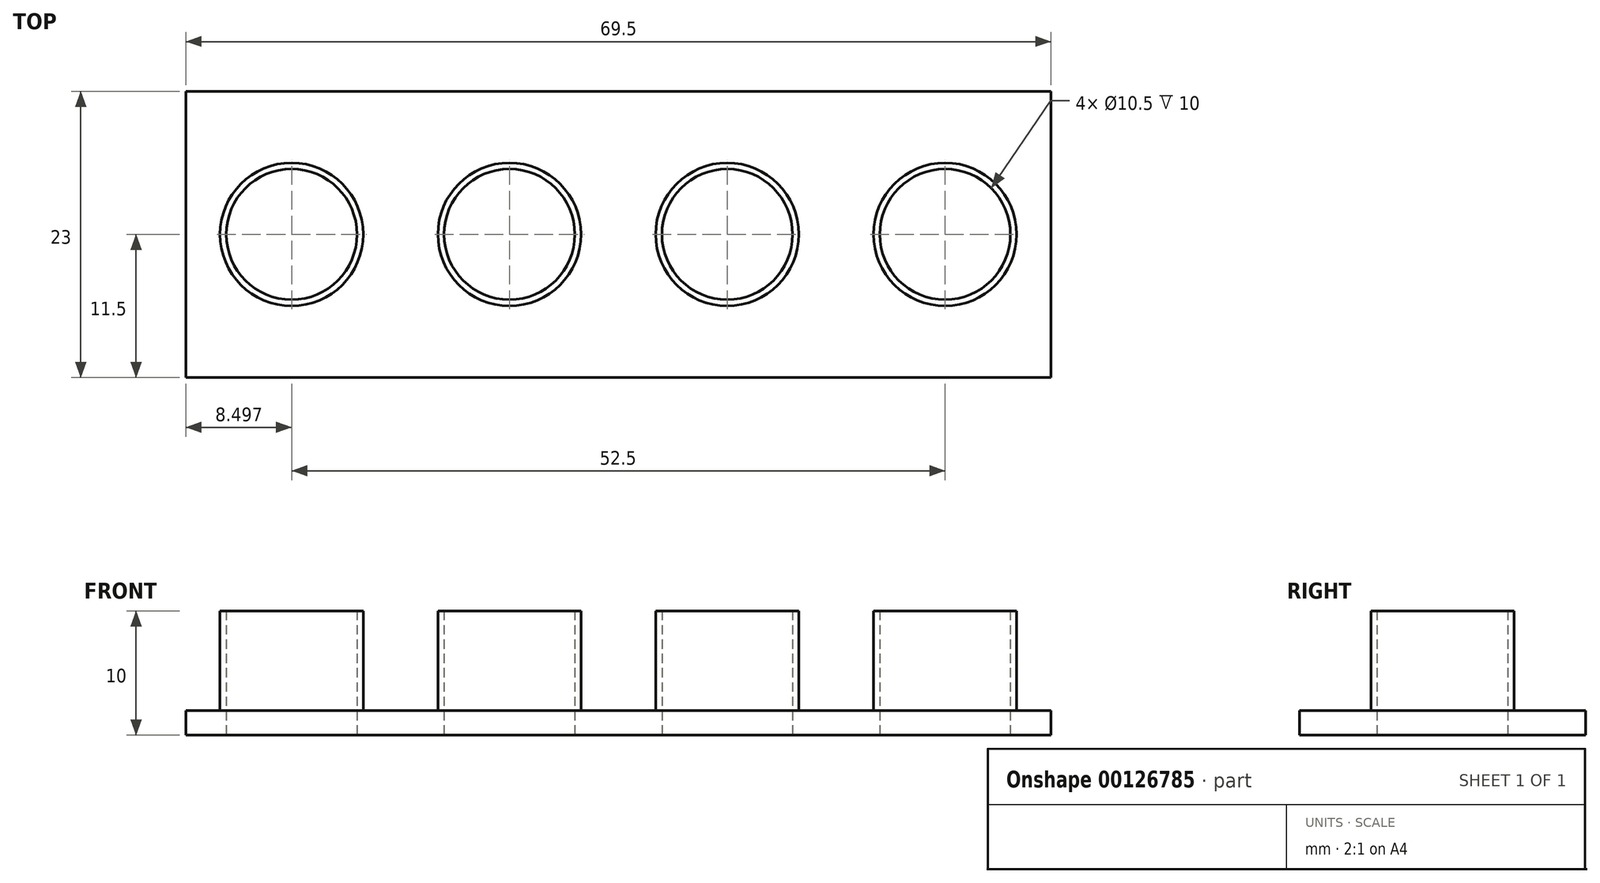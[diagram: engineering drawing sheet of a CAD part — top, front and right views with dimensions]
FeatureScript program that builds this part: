
annotation { "Feature Type Name" : "Feature", "Feature Type Description" : "" }
export const myFeature = defineFeature(function(context is Context, id is Id, definition is map)
    precondition{}
    {
        {
            var Q0;
            Q0=qCreatedBy(makeId("Top.planeOp"),FACE);
            var sketch = newSketch(context, id + "F0", { "sketchPlane" : qUnion([Q0])});
            skLineSegment(sketch, "E0.bottom", {"start": v(-29.8, 7) * mm, "end": v(-15.8, 7) * mm});
            skLineSegment(sketch, "E0.top", {"start": v(-29.8, -13) * mm, "end": v(-15.8, -13) * mm});
            skLineSegment(sketch, "E0.left", {"start": v(-29.8, 7) * mm, "end": v(-29.8, -13) * mm});
            skLineSegment(sketch, "E0.right", {"start": v(36.7, 7) * mm, "end": v(36.7, -13) * mm});
            skLineSegment(sketch, "E1.top", {"start": v(-15.8, 3) * mm, "end": v(-14.8, 3) * mm});
            skLineSegment(sketch, "E1.left", {"start": v(-15.8, 7) * mm, "end": v(-15.8, 3) * mm});
            skLineSegment(sketch, "E1.right", {"start": v(-14.8, 7) * mm, "end": v(-14.8, 3) * mm});
            skLineSegment(sketch, "E2.top", {"start": v(-13.3, 3) * mm, "end": v(-12.3, 3) * mm});
            skLineSegment(sketch, "E2.left", {"start": v(-13.3, 7) * mm, "end": v(-13.3, 3) * mm});
            skLineSegment(sketch, "E2.right", {"start": v(-12.3, 7) * mm, "end": v(-12.3, 3) * mm});
            skLineSegment(sketch, "E3.top", {"start": v(4.2, 3) * mm, "end": v(5.2, 3) * mm});
            skLineSegment(sketch, "E3.left", {"start": v(4.2, 7) * mm, "end": v(4.2, 3) * mm});
            skLineSegment(sketch, "E3.right", {"start": v(5.2, 7) * mm, "end": v(5.2, 3) * mm});
            skLineSegment(sketch, "E4.top", {"start": v(19.2, 3) * mm, "end": v(20.2, 3) * mm});
            skLineSegment(sketch, "E4.left", {"start": v(19.2, 7) * mm, "end": v(19.2, 3) * mm});
            skLineSegment(sketch, "E4.right", {"start": v(20.2, 7) * mm, "end": v(20.2, 3) * mm});
            skLineSegment(sketch, "E5.top", {"start": v(21.7, 3) * mm, "end": v(22.7, 3) * mm});
            skLineSegment(sketch, "E5.left", {"start": v(21.7, 7) * mm, "end": v(21.7, 3) * mm});
            skLineSegment(sketch, "E5.right", {"start": v(22.7, 7) * mm, "end": v(22.7, 3) * mm});
            skLineSegment(sketch, "E6.top", {"start": v(-15.8, -9) * mm, "end": v(-14.8, -9) * mm});
            skLineSegment(sketch, "E6.left", {"start": v(-15.8, -13) * mm, "end": v(-15.8, -9) * mm});
            skLineSegment(sketch, "E6.right", {"start": v(-14.8, -13) * mm, "end": v(-14.8, -9) * mm});
            skLineSegment(sketch, "E7.top", {"start": v(-13.3, -9) * mm, "end": v(-12.3, -9) * mm});
            skLineSegment(sketch, "E7.left", {"start": v(-13.3, -13) * mm, "end": v(-13.3, -9) * mm});
            skLineSegment(sketch, "E7.right", {"start": v(-12.3, -13) * mm, "end": v(-12.3, -9) * mm});
            skLineSegment(sketch, "E8.top", {"start": v(1.7, -9) * mm, "end": v(2.7, -9) * mm});
            skLineSegment(sketch, "E8.left", {"start": v(1.7, -13) * mm, "end": v(1.7, -9) * mm});
            skLineSegment(sketch, "E8.right", {"start": v(2.7, -13) * mm, "end": v(2.7, -9) * mm});
            skLineSegment(sketch, "E9.top", {"start": v(4.2, -9) * mm, "end": v(5.2, -9) * mm});
            skLineSegment(sketch, "E9.left", {"start": v(4.2, -13) * mm, "end": v(4.2, -9) * mm});
            skLineSegment(sketch, "E9.right", {"start": v(5.2, -13) * mm, "end": v(5.2, -9) * mm});
            skLineSegment(sketch, "E10.top", {"start": v(19.2, -9) * mm, "end": v(20.2, -9) * mm});
            skLineSegment(sketch, "E10.left", {"start": v(19.2, -13) * mm, "end": v(19.2, -9) * mm});
            skLineSegment(sketch, "E10.right", {"start": v(20.2, -13) * mm, "end": v(20.2, -9) * mm});
            skLineSegment(sketch, "E11.top", {"start": v(21.7, -9) * mm, "end": v(22.7, -9) * mm});
            skLineSegment(sketch, "E11.left", {"start": v(21.7, -13) * mm, "end": v(21.7, -9) * mm});
            skLineSegment(sketch, "E11.right", {"start": v(22.7, -13) * mm, "end": v(22.7, -9) * mm});
            skLineSegment(sketch, "E12.top", {"start": v(1.7, 3) * mm, "end": v(2.7, 3) * mm});
            skLineSegment(sketch, "E12.left", {"start": v(1.7, 7) * mm, "end": v(1.7, 3) * mm});
            skLineSegment(sketch, "E12.right", {"start": v(2.7, 7) * mm, "end": v(2.7, 3) * mm});
            skLineSegment(sketch, "E13.trimOffspring", {"start": v(-14.8, 7) * mm, "end": v(-13.3, 7) * mm});
            skLineSegment(sketch, "E14.trimOffspring", {"start": v(-12.3, 7) * mm, "end": v(1.7, 7) * mm});
            skLineSegment(sketch, "E15.trimOffspring", {"start": v(2.7, 7) * mm, "end": v(4.2, 7) * mm});
            skLineSegment(sketch, "E16.trimOffspring", {"start": v(5.2, 7) * mm, "end": v(19.2, 7) * mm});
            skLineSegment(sketch, "E17.trimOffspring", {"start": v(-14.8, -13) * mm, "end": v(-13.3, -13) * mm});
            skLineSegment(sketch, "E18.trimOffspring", {"start": v(-12.3, -13) * mm, "end": v(1.7, -13) * mm});
            skLineSegment(sketch, "E19.trimOffspring", {"start": v(2.7, -13) * mm, "end": v(4.2, -13) * mm});
            skLineSegment(sketch, "E20.trimOffspring", {"start": v(5.2, -13) * mm, "end": v(19.2, -13) * mm});
            skLineSegment(sketch, "E21.trimOffspring", {"start": v(20.2, -13) * mm, "end": v(21.7, -13) * mm});
            skLineSegment(sketch, "E22.trimOffspring", {"start": v(22.7, -13) * mm, "end": v(36.7, -13) * mm});
            skLineSegment(sketch, "E23.trimOffspring", {"start": v(20.2, 7) * mm, "end": v(21.7, 7) * mm});
            skLineSegment(sketch, "E24.trimOffspring", {"start": v(22.7, 7) * mm, "end": v(36.7, 7) * mm});
            skLineSegment(sketch, "E25", {"start": v(-29.8, -3) * mm, "end": v(37.18, -3) * mm, "construction": true});
            skLineSegment(sketch, "E26", {"start": v(-22.8, 7) * mm, "end": v(-22.8, -26.1) * mm, "construction": true});
            skLineSegment(sketch, "E27", {"start": v(-5.3, 7) * mm, "end": v(-5.3, -26.98) * mm, "construction": true});
            skLineSegment(sketch, "E28", {"start": v(12.2, 7) * mm, "end": v(12.2, -27.86) * mm, "construction": true});
            skLineSegment(sketch, "E29", {"start": v(29.7, 7) * mm, "end": v(29.7, -23.35) * mm, "construction": true});
            skCircle(sketch, "E30", {"center": v(-22.8, -3) * mm, "radius": 5.25 * mm});
            skCircle(sketch, "E31", {"center": v(-22.8, -3) * mm, "radius": 5.75 * mm});
            skCircle(sketch, "E32", {"center": v(-5.3, -3) * mm, "radius": 5.75 * mm});
            skCircle(sketch, "E33", {"center": v(-5.3, -3) * mm, "radius": 5.25 * mm});
            skCircle(sketch, "E34", {"center": v(12.2, -3) * mm, "radius": 5.75 * mm});
            skCircle(sketch, "E35", {"center": v(12.2, -3) * mm, "radius": 5.25 * mm});
            skCircle(sketch, "E36", {"center": v(29.7, -3) * mm, "radius": 5.75 * mm});
            skCircle(sketch, "E37", {"center": v(29.7, -3) * mm, "radius": 5.25 * mm});
            skLineSegment(sketch, "E38.bottom", {"start": v(-31.3, 8.5) * mm, "end": v(38.2, 8.5) * mm});
            skLineSegment(sketch, "E38.top", {"start": v(-31.3, -14.5) * mm, "end": v(38.2, -14.5) * mm});
            skLineSegment(sketch, "E38.left", {"start": v(-31.3, 8.5) * mm, "end": v(-31.3, -14.5) * mm});
            skLineSegment(sketch, "E38.right", {"start": v(38.2, 8.5) * mm, "end": v(38.2, -14.5) * mm});
            skLineSegment(sketch, "E39", {"start": v(-15.8, 7) * mm, "end": v(-14.8, 7) * mm});
            skLineSegment(sketch, "E40", {"start": v(-13.3, 7) * mm, "end": v(-12.3, 7) * mm});
            skLineSegment(sketch, "E41", {"start": v(1.7, 7) * mm, "end": v(2.7, 7) * mm});
            skLineSegment(sketch, "E42", {"start": v(4.2, 7) * mm, "end": v(5.2, 7) * mm});
            skLineSegment(sketch, "E43", {"start": v(-15.8, -13) * mm, "end": v(-14.8, -13) * mm});
            skLineSegment(sketch, "E44", {"start": v(-13.3, -13) * mm, "end": v(-12.3, -13) * mm});
            skLineSegment(sketch, "E45", {"start": v(1.7, -13) * mm, "end": v(2.7, -13) * mm});
            skLineSegment(sketch, "E46", {"start": v(4.3, -13.03) * mm, "end": v(5.2, -13) * mm});
            skLineSegment(sketch, "E47", {"start": v(19.2, 7) * mm, "end": v(20.2, 7) * mm});
            skLineSegment(sketch, "E48", {"start": v(21.7, 7) * mm, "end": v(22.7, 7) * mm});
            skLineSegment(sketch, "E49", {"start": v(19.2, -13) * mm, "end": v(20.2, -13) * mm});
            skLineSegment(sketch, "E50", {"start": v(21.7, -13) * mm, "end": v(22.7, -13) * mm});
            skSolve(sketch);
        }
        {
            var Q0;
            Q0=makeQuery(id+"F0.imprint","IMPRINT",FACE,{"disambiguationData":[TD([[makeQuery(id+"F0.imprint","IMPRINT",EDGE,{"derivedFrom":sQuery(id+"F0.wireOp",EDGE,"E0.bottom")}),-1.0]])]});
            var Q1;
            Q1=makeQuery(id+"F0.imprint","IMPRINT",FACE,{"disambiguationData":[TD([[makeQuery(id+"F0.imprint","IMPRINT",EDGE,{"derivedFrom":sQuery(id+"F0.wireOp",EDGE,"E1.top")}),1.0]])]});
            var Q2;
            Q2=makeQuery(id+"F0.imprint","IMPRINT",FACE,{"disambiguationData":[TD([[makeQuery(id+"F0.imprint","IMPRINT",EDGE,{"derivedFrom":sQuery(id+"F0.wireOp",EDGE,"E2.top")}),1.0]])]});
            var Q3;
            Q3=makeQuery(id+"F0.imprint","IMPRINT",FACE,{"disambiguationData":[TD([[makeQuery(id+"F0.imprint","IMPRINT",EDGE,{"derivedFrom":sQuery(id+"F0.wireOp",EDGE,"E12.top")}),1.0]])]});
            var Q4;
            Q4=makeQuery(id+"F0.imprint","IMPRINT",FACE,{"disambiguationData":[TD([[makeQuery(id+"F0.imprint","IMPRINT",EDGE,{"derivedFrom":sQuery(id+"F0.wireOp",EDGE,"E3.top")}),1.0]])]});
            var Q5;
            Q5=makeQuery(id+"F0.imprint","IMPRINT",FACE,{"disambiguationData":[TD([[makeQuery(id+"F0.imprint","IMPRINT",EDGE,{"derivedFrom":sQuery(id+"F0.wireOp",EDGE,"E4.top")}),1.0]])]});
            var Q6;
            Q6=makeQuery(id+"F0.imprint","IMPRINT",FACE,{"disambiguationData":[TD([[makeQuery(id+"F0.imprint","IMPRINT",EDGE,{"derivedFrom":sQuery(id+"F0.wireOp",EDGE,"E5.top")}),1.0]])]});
            var Q7;
            Q7=makeQuery(id+"F0.imprint","IMPRINT",FACE,{"disambiguationData":[TD([[makeQuery(id+"F0.imprint","IMPRINT",EDGE,{"derivedFrom":sQuery(id+"F0.wireOp",EDGE,"E6.top")}),-1.0]])]});
            var Q8;
            Q8=makeQuery(id+"F0.imprint","IMPRINT",FACE,{"disambiguationData":[TD([[makeQuery(id+"F0.imprint","IMPRINT",EDGE,{"derivedFrom":sQuery(id+"F0.wireOp",EDGE,"E7.top")}),-1.0]])]});
            var Q9;
            Q9=makeQuery(id+"F0.imprint","IMPRINT",FACE,{"disambiguationData":[TD([[makeQuery(id+"F0.imprint","IMPRINT",EDGE,{"derivedFrom":sQuery(id+"F0.wireOp",EDGE,"E8.top")}),-1.0]])]});
            var Q10;
            Q10=makeQuery(id+"F0.imprint","IMPRINT",FACE,{"disambiguationData":[TD([[makeQuery(id+"F0.imprint","IMPRINT",EDGE,{"derivedFrom":sQuery(id+"F0.wireOp",EDGE,"E0.bottom")}),1.0]])]});
            var Q11;
            Q11=makeQuery(id+"F0.imprint","IMPRINT",FACE,{"disambiguationData":[TD([[makeQuery(id+"F0.imprint","IMPRINT",EDGE,{"derivedFrom":sQuery(id+"F0.wireOp",EDGE,"E10.top")}),-1.0]])]});
            var Q12;
            Q12=makeQuery(id+"F0.imprint","IMPRINT",FACE,{"disambiguationData":[TD([[makeQuery(id+"F0.imprint","IMPRINT",EDGE,{"derivedFrom":sQuery(id+"F0.wireOp",EDGE,"E11.top")}),-1.0]])]});
            extrude(context, id + "F1", {"entities" : qUnion([Q0, Q1, Q2, Q3, Q4, Q5, Q6, Q7, Q8, Q9, Q10, Q11, Q12]), "depth" : 2 * mm});
        }
        {
            var Q0;
            Q0=makeQuery(id+"F0.imprint","IMPRINT",FACE,{"disambiguationData":[TD([[makeQuery(id+"F0.imprint","IMPRINT",EDGE,{"derivedFrom":sQuery(id+"F0.wireOp",EDGE,"E30")}),-1.0]])]});
            var Q1;
            Q1=makeQuery(id+"F0.imprint","IMPRINT",FACE,{"disambiguationData":[TD([[makeQuery(id+"F0.imprint","IMPRINT",EDGE,{"derivedFrom":sQuery(id+"F0.wireOp",EDGE,"E32")}),1.0]])]});
            var Q2;
            Q2=makeQuery(id+"F0.imprint","IMPRINT",FACE,{"disambiguationData":[TD([[makeQuery(id+"F0.imprint","IMPRINT",EDGE,{"derivedFrom":sQuery(id+"F0.wireOp",EDGE,"E34")}),1.0]])]});
            var Q3;
            Q3=makeQuery(id+"F0.imprint","IMPRINT",FACE,{"disambiguationData":[TD([[makeQuery(id+"F0.imprint","IMPRINT",EDGE,{"derivedFrom":sQuery(id+"F0.wireOp",EDGE,"E36")}),1.0]])]});
            extrude(context, id + "F2", {"entities" : qUnion([Q0, Q1, Q2, Q3]), "operationType" : NewBodyOperationType.ADD, "depth" : 10 * mm});
        }
    });
